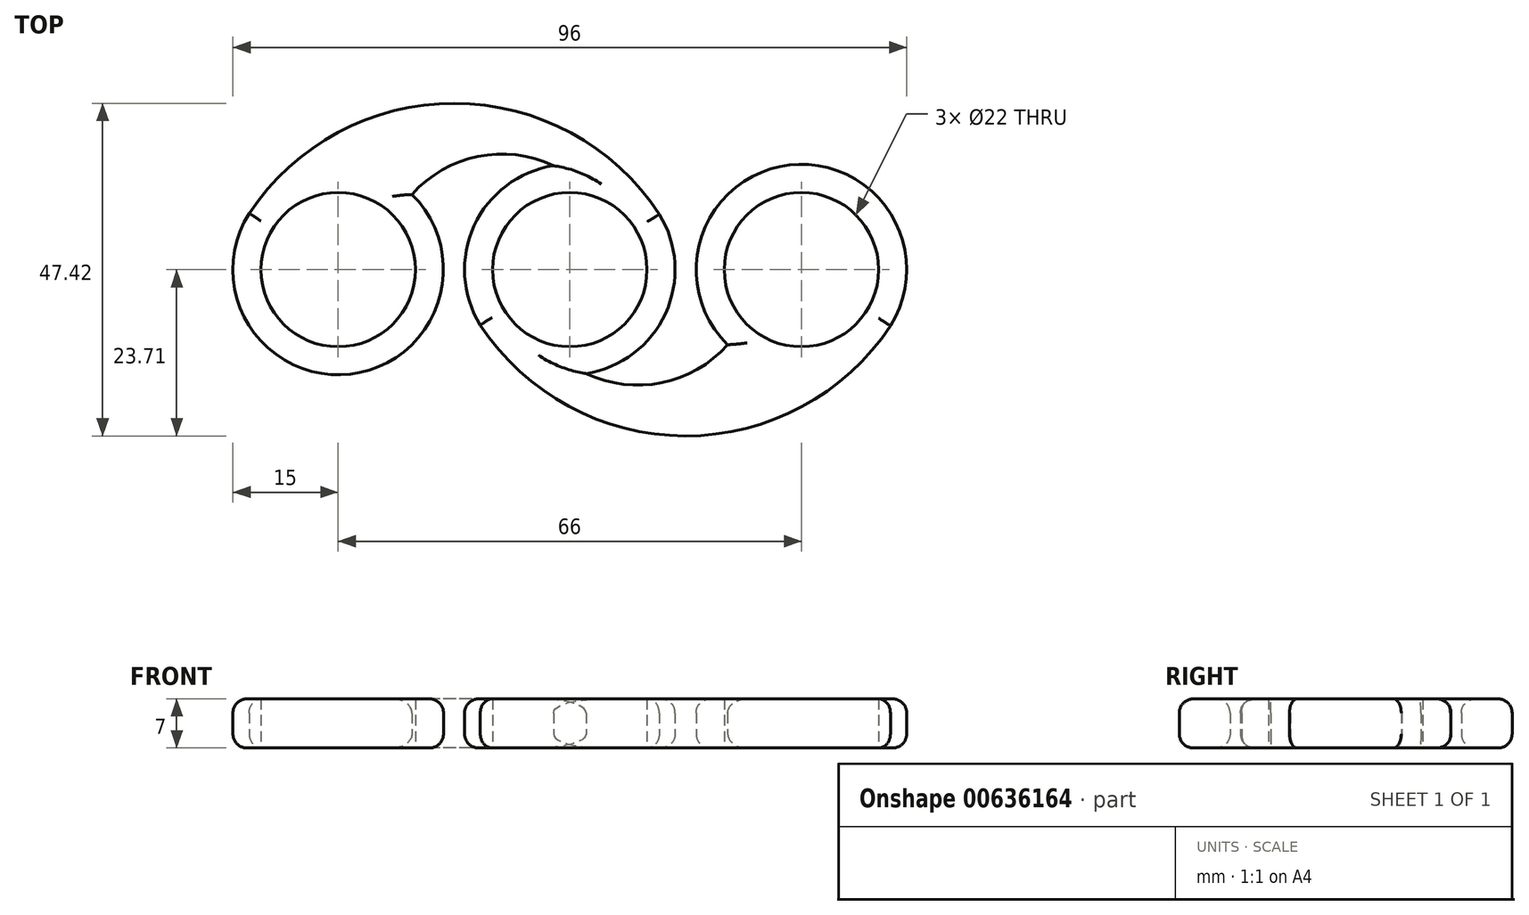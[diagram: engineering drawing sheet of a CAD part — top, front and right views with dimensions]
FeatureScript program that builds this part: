
annotation { "Feature Type Name" : "Feature", "Feature Type Description" : "" }
export const myFeature = defineFeature(function(context is Context, id is Id, definition is map)
    precondition{}
    {
        {
            var Q0;
            Q0=qCreatedBy(makeId("Top.planeOp"),FACE);
            var sketch = newSketch(context, id + "F0", { "sketchPlane" : qUnion([Q0])});
            skCircle(sketch, "E0", {"center": v(0, 0) * mm, "radius": 11 * mm});
            skCircle(sketch, "E1", {"center": v(0, 0) * mm, "radius": 15 * mm});
            skCircle(sketch, "E2.1.0.0", {"center": v(33, 0) * mm, "radius": 15 * mm});
            skCircle(sketch, "E2.1.0.1", {"center": v(33, 0) * mm, "radius": 11 * mm});
            skCircle(sketch, "E2.2.0.0", {"center": v(66, 0) * mm, "radius": 15 * mm});
            skCircle(sketch, "E2.2.0.1", {"center": v(66, 0) * mm, "radius": 11 * mm});
            skLineSegment(sketch, "E2.direction1", {"start": v(0, 0) * mm, "end": v(33, 0) * mm, "construction": true});
            skArc(sketch, "E3", {"start": v(45.75, 7.9) * mm, "mid": v(16.57, 23.71) * mm, "end": v(-12.68, 8.01) * mm});
            skArc(sketch, "E4", {"start": v(30.68, 14.82) * mm, "mid": v(19.9, 16.13) * mm, "end": v(10.5, 10.7) * mm});
            skArc(sketch, "E5.1.0", {"start": v(20.25, -7.9) * mm, "mid": v(49.43, -23.71) * mm, "end": v(78.68, -8.01) * mm});
            skArc(sketch, "E5.1.1", {"start": v(35.32, -14.82) * mm, "mid": v(46.1, -16.13) * mm, "end": v(55.5, -10.7) * mm});
            skSolve(sketch);
        }
        {
            var Q0;
            {var subQ0=sQuery(id+"F0.wireOp",EDGE,"E5.1.1");Q0=makeQuery(id+"F0.imprint","IMPRINT",FACE,{"disambiguationData":[TD([[makeQuery(id+"F0.imprint","IMPRINT",EDGE,{"derivedFrom":subQ0}),-1.0]])]});}
            var Q1;
            Q1=makeQuery(id+"F0.imprint","IMPRINT",FACE,{"disambiguationData":[TD([[makeQuery(id+"F0.imprint","IMPRINT",EDGE,{"derivedFrom":sQuery(id+"F0.wireOp",EDGE,"E2.2.0.1")}),-1.0]])]});
            var Q2;
            Q2=makeQuery(id+"F0.imprint","IMPRINT",FACE,{"disambiguationData":[TD([[makeQuery(id+"F0.imprint","IMPRINT",EDGE,{"derivedFrom":sQuery(id+"F0.wireOp",EDGE,"E2.1.0.1")}),-1.0]])]});
            var Q3;
            {var subQ0=sQuery(id+"F0.wireOp",EDGE,"E4");Q3=makeQuery(id+"F0.imprint","IMPRINT",FACE,{"disambiguationData":[TD([[makeQuery(id+"F0.imprint","IMPRINT",EDGE,{"derivedFrom":subQ0}),-1.0]])]});}
            var Q4;
            Q4=makeQuery(id+"F0.imprint","IMPRINT",FACE,{"disambiguationData":[TD([[makeQuery(id+"F0.imprint","IMPRINT",EDGE,{"derivedFrom":sQuery(id+"F0.wireOp",EDGE,"E0")}),-1.0]])]});
            extrude(context, id + "F1", {"entities" : qUnion([Q0, Q1, Q2, Q3, Q4]), "depth" : 7 * mm, "offsetDistance" : 25 * mm});
        }
        {
            var Q0;
            Q0=makeQuery(id+"F1.opExtrude","CAP_EDGE",EDGE,{"disambiguationData":[OSD([sQuery(id+"F0.wireOp",EDGE,"E3")])],"isStart":false});
            var Q1;
            Q1=makeQuery(id+"F1.opExtrude","CAP_EDGE",EDGE,{"disambiguationData":[OSD([sQuery(id+"F0.wireOp",EDGE,"E4")])],"isStart":false});
            var Q2;
            Q2=makeQuery(id+"F1.opExtrude","CAP_EDGE",EDGE,{"disambiguationData":[OSD([sQuery(id+"F0.wireOp",EDGE,"E1")])],"isStart":false});
            var Q3;
            {var subQ0=sQuery(id+"F0.wireOp",EDGE,"E2.1.0.0");Q3=makeQuery(id+"F1.opExtrude","CAP_EDGE",EDGE,{"disambiguationData":[OSD([subQ0]),TDD([makeQuery(id+"F0.imprint","IMPRINT",EDGE,{"disambiguationData":[TD([[makeQuery(id+"F0.imprint","INTERSECT",VERTEX,{"derivedFrom":[subQ0,sQuery(id+"F0.wireOp",EDGE,"E4")]}),-1.0]])],"derivedFrom":subQ0})])],"isStart":false});}
            var Q4;
            Q4=makeQuery(id+"F1.opExtrude","CAP_EDGE",EDGE,{"disambiguationData":[OSD([sQuery(id+"F0.wireOp",EDGE,"E5.1.0")])],"isStart":false});
            var Q5;
            Q5=makeQuery(id+"F1.opExtrude","CAP_EDGE",EDGE,{"disambiguationData":[OSD([sQuery(id+"F0.wireOp",EDGE,"E2.2.0.0")])],"isStart":false});
            var Q6;
            Q6=makeQuery(id+"F1.opExtrude","CAP_EDGE",EDGE,{"disambiguationData":[OSD([sQuery(id+"F0.wireOp",EDGE,"E5.1.1")])],"isStart":false});
            var Q7;
            {var subQ0=sQuery(id+"F0.wireOp",EDGE,"E2.1.0.0");Q7=makeQuery(id+"F1.opExtrude","CAP_EDGE",EDGE,{"disambiguationData":[OSD([subQ0]),TDD([makeQuery(id+"F0.imprint","IMPRINT",EDGE,{"disambiguationData":[TD([[makeQuery(id+"F0.imprint","INTERSECT",VERTEX,{"disambiguationData":[OD(0.0)],"derivedFrom":[subQ0,sQuery(id+"F0.wireOp",EDGE,"E3")]}),1.0]])],"derivedFrom":subQ0})])],"isStart":false});}
            var Q8;
            Q8=makeQuery(id+"F1.opExtrude","CAP_EDGE",EDGE,{"disambiguationData":[OSD([sQuery(id+"F0.wireOp",EDGE,"E5.1.0")])],"isStart":true});
            var Q9;
            Q9=makeQuery(id+"F1.opExtrude","CAP_EDGE",EDGE,{"disambiguationData":[OSD([sQuery(id+"F0.wireOp",EDGE,"E5.1.1")])],"isStart":true});
            var Q10;
            Q10=makeQuery(id+"F1.opExtrude","CAP_EDGE",EDGE,{"disambiguationData":[OSD([sQuery(id+"F0.wireOp",EDGE,"E2.2.0.0")])],"isStart":true});
            var Q11;
            {var subQ0=sQuery(id+"F0.wireOp",EDGE,"E2.1.0.0");Q11=makeQuery(id+"F1.opExtrude","CAP_EDGE",EDGE,{"disambiguationData":[OSD([subQ0]),TDD([makeQuery(id+"F0.imprint","IMPRINT",EDGE,{"disambiguationData":[TD([[makeQuery(id+"F0.imprint","INTERSECT",VERTEX,{"disambiguationData":[OD(0.0)],"derivedFrom":[subQ0,sQuery(id+"F0.wireOp",EDGE,"E3")]}),1.0]])],"derivedFrom":subQ0})])],"isStart":true});}
            var Q12;
            Q12=makeQuery(id+"F1.opExtrude","CAP_EDGE",EDGE,{"disambiguationData":[OSD([sQuery(id+"F0.wireOp",EDGE,"E3")])],"isStart":true});
            var Q13;
            Q13=makeQuery(id+"F1.opExtrude","CAP_EDGE",EDGE,{"disambiguationData":[OSD([sQuery(id+"F0.wireOp",EDGE,"E1")])],"isStart":true});
            var Q14;
            Q14=makeQuery(id+"F1.opExtrude","CAP_EDGE",EDGE,{"disambiguationData":[OSD([sQuery(id+"F0.wireOp",EDGE,"E4")])],"isStart":true});
            var Q15;
            {var subQ0=sQuery(id+"F0.wireOp",EDGE,"E2.1.0.0");Q15=makeQuery(id+"F1.opExtrude","CAP_EDGE",EDGE,{"disambiguationData":[OSD([subQ0]),TDD([makeQuery(id+"F0.imprint","IMPRINT",EDGE,{"disambiguationData":[TD([[makeQuery(id+"F0.imprint","INTERSECT",VERTEX,{"derivedFrom":[subQ0,sQuery(id+"F0.wireOp",EDGE,"E4")]}),-1.0]])],"derivedFrom":subQ0})])],"isStart":true});}
            fillet(context, id + "F2", {"entities" : qUnion([Q0, Q1, Q2, Q3, Q4, Q5, Q6, Q7, Q8, Q9, Q10, Q11, Q12, Q13, Q14, Q15]), "radius" : 2 * mm, "tangentPropagation" : true, "allowEdgeOverflow" : false});
        }
    });
